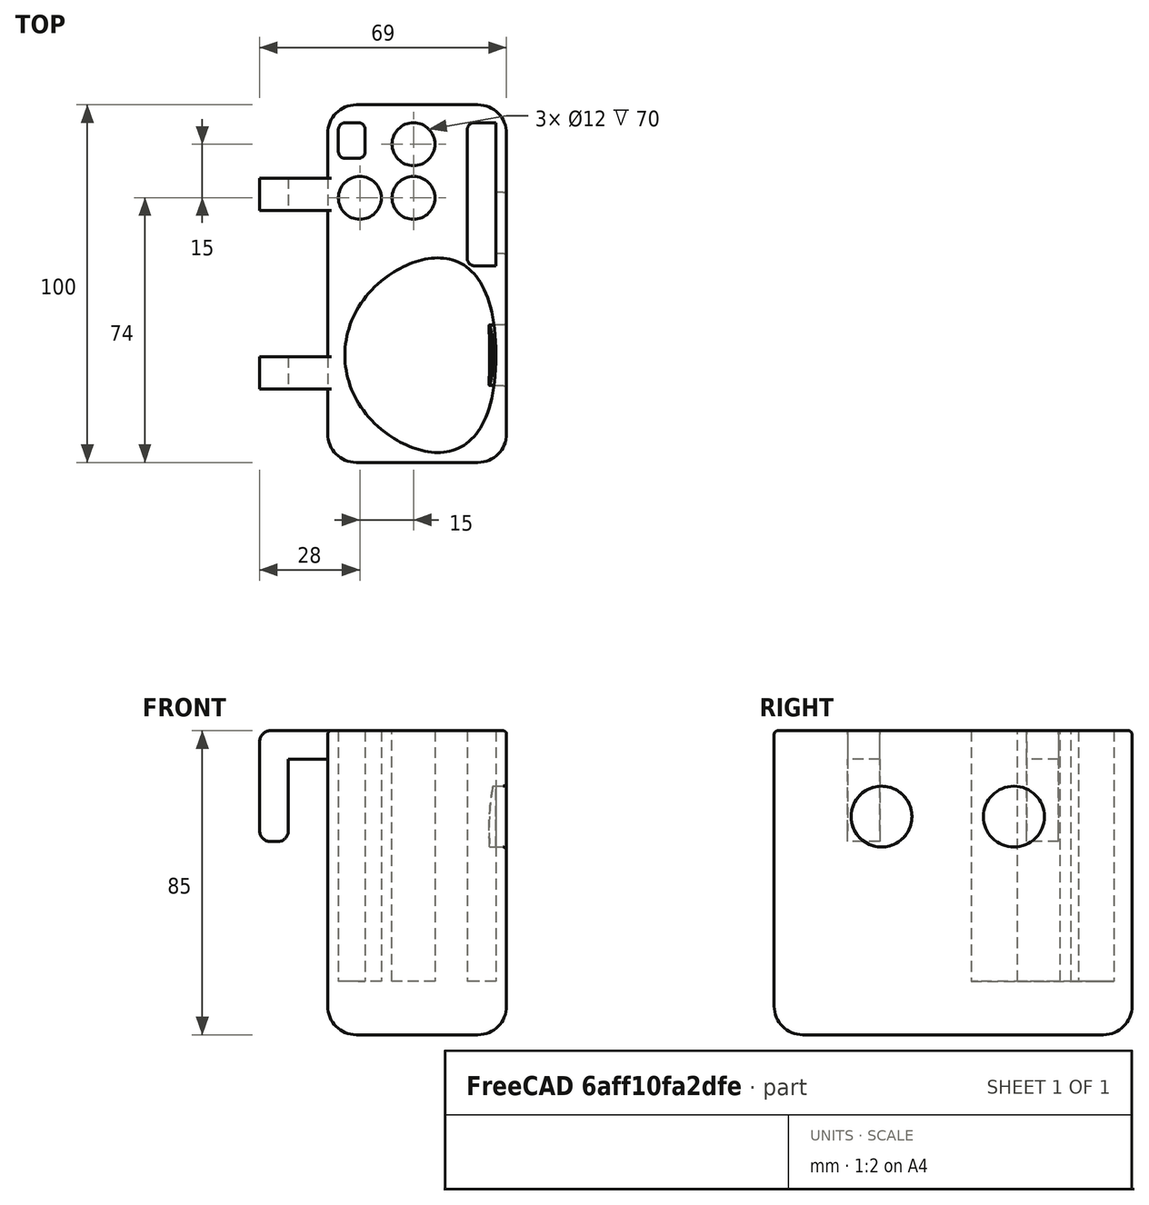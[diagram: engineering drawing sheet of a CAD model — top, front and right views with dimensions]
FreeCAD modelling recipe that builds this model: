
FCSTD DOCUMENT  (FreeCAD 0.20R29177 +426 (Git))
Label: RemoteHolder
License: All rights reserved
LicenseURL: http://en.wikipedia.org/wiki/All_rights_reserved
objects: Sketcher::SketchObject×6, PartDesign::Pocket×5, PartDesign::Fillet×2, Part::Box×1, PartDesign::FeatureBase×1, PartDesign::Pad×1, PartDesign::Body×1, Mesh::Feature×1
note: 25 computed .brp shape members not serialized (recipe doc carries the construction recipe); baked Part::Feature solids carry a one-line shape summary decoded from their .brp

FEATURE [Part::Box] Box  label="Cube"
  AttacherType = Attacher::AttachEngine3D
  Height = 85
  Length = 50
  Width = 100
FEATURE [PartDesign::FeatureBase] BaseFeature
  BaseFeature = -> Box
FEATURE [Sketcher::SketchObject] Sketch
  FullyConstrained = true
  MapMode = 5
  Placement = pos=(0,0,85) rot=(0,0,1;0rad)
  Support = -> [BaseFeature]
  sketch-geometry (15):
    g0-g5: Circle x6 (B-spline internal-alignment scaffolding for g6; pole/knot coordinates omitted)
    g6: BSplineCurve PolesCount=6 KnotsCount=4 Degree=3 IsPeriodic=0
    g7-g10: GeomPoint x4 (B-spline internal-alignment scaffolding for g6; pole/knot coordinates omitted)
    g11: LineSegment StartX=47 StartY=65 StartZ=0 EndX=47 EndY=30 EndZ=0
    g12: LineSegment StartX=47 StartY=30 StartZ=0 EndX=47 EndY=-5 EndZ=0
    g13: LineSegment StartX=47 StartY=30 StartZ=0 EndX=2 EndY=55 EndZ=0
    g14: LineSegment StartX=47 StartY=30 StartZ=0 EndX=2 EndY=5 EndZ=0
  constraints (23):
    c: Equal(g0, g1-g5) x5
    c: Coincident(g6,g0)
    c: InternalAlignment(g0-g5 -> g6) x6
    c: InternalAlignment(g7-g10 -> g6) x4
    c: Vertical(g2,g3)
    c: Vertical(g11)
    c: Coincident(g12,g6)
    c: Coincident(g12,g1)
    c: Vertical(g12)
    c: Coincident(g13,g6)
    c: Coincident(g13,g3)
    c: Coincident(g14,g6)
    c: Coincident(g14,g2)
    c: Equal(g13,g14)
    c: Equal(g11,g12)
    c: Coincident(g11,g6)
    c: Coincident(g11,g4)
    c: DistanceX(g2,g1) = 45
    c: DistanceY(g2,g3) = 50
    c: Weight(g0) = 1
    c: DistanceY(g-1,g2) = 5
    c: DistanceY(g1,g4) = 70
    c: DistanceX(g-1,g2) = 2
FEATURE [Sketcher::SketchObject] Sketch002
  FullyConstrained = true
  MapMode = 5
  Placement = pos=(0,0,85) rot=(0,0,1;0rad)
  Support = -> [BaseFeature]
  sketch-geometry (8):
    g0: LineSegment StartX=47 StartY=95 StartZ=0 EndX=41 EndY=95 EndZ=0
    g1: LineSegment StartX=39 StartY=93 StartZ=0 EndX=39 EndY=57 EndZ=0
    g2: LineSegment StartX=41 StartY=55 StartZ=0 EndX=47 EndY=55 EndZ=0
    g3: LineSegment StartX=47 StartY=55 StartZ=0 EndX=47 EndY=95 EndZ=0
    g4: ArcOfCircle CenterX=41 CenterY=93 CenterZ=0 NormalX=0 NormalY=0 NormalZ=1 AngleXU=0 Radius=2 StartAngle=1.5708 EndAngle=3.14159
    g5: GeomPoint X=39 Y=95 Z=0
    g6: ArcOfCircle CenterX=41 CenterY=57 CenterZ=0 NormalX=0 NormalY=0 NormalZ=1 AngleXU=0 Radius=2 StartAngle=3.14159 EndAngle=4.71239
    g7: GeomPoint X=39 Y=55 Z=0
  constraints (20):
    c: Coincident(g2,g3)
    c: Coincident(g3,g0)
    c: Horizontal(g0)
    c: Horizontal(g2)
    c: Vertical(g1)
    c: Vertical(g3)
    c: DistanceX(g5,g0) = 8
    c: DistanceY(g-1,g0) = 95
    c: DistanceX(g-1,g2) = 47
    c: DistanceY(g3,g3) = 40
    c: PointOnObject(g5,g0)
    c: PointOnObject(g5,g1)
    c: Tangent(g0,g4) = -1.5708
    c: Tangent(g1,g4) = -1.5708
    c: PointOnObject(g7,g1)
    c: PointOnObject(g7,g2)
    c: Tangent(g1,g6) = -1.5708
    c: Tangent(g2,g6) = -1.5708
    c: Equal(g4,g6)
    c: Radius(g4) = 2
FEATURE [PartDesign::Pocket] Pocket002
  BaseFeature = -> BaseFeature
  Direction = (0,0,-1)
  Length = 70
  Length2 = 5
  Profile = -> Sketch002
  ReferenceAxis = -> Sketch002 [N_Axis]
  Type = 0
FEATURE [PartDesign::Pocket] Pocket
  BaseFeature = -> Pocket002
  Direction = (0,0,-1)
  Length = 80
  Length2 = 5
  Profile = -> Sketch
  ReferenceAxis = -> Sketch [N_Axis]
  TaperAngle = -3
  Type = 0
FEATURE [Sketcher::SketchObject] Sketch001
  FullyConstrained = true
  MapMode = 5
  Placement = pos=(50,0,0) rot=(0.57735,0.57735,0.57735;2.0944rad)
  Support = -> [Pocket]
  sketch-geometry (2):
    g0: Circle CenterX=30 CenterY=61 CenterZ=0 NormalX=0 NormalY=0 NormalZ=1 AngleXU=0 Radius=8.5
    g1: Circle CenterX=67 CenterY=61 CenterZ=0 NormalX=0 NormalY=0 NormalZ=1 AngleXU=0 Radius=8.5
  constraints (6):
    c: Diameter(g0) = 17
    c: DistanceY(g-1,g0) = 61
    c: DistanceX(g-1,g0) = 30
    c: Diameter(g1) = 17
    c: DistanceY(g-1,g1) = 61
    c: DistanceX(g-1,g1) = 67
FEATURE [PartDesign::Pocket] Pocket001
  BaseFeature = -> Pocket
  Direction = (-1,0,0)
  Length = 7
  Length2 = 5
  Profile = -> Sketch001
  ReferenceAxis = -> Sketch001 [N_Axis]
  Type = 0
FEATURE [Sketcher::SketchObject] Sketch003
  FullyConstrained = true
  MapMode = 5
  Placement = pos=(0,0,85) rot=(0,0,1;0rad)
  Support = -> [Box]
  sketch-geometry (15):
    g0: ArcOfCircle CenterX=5 CenterY=93 CenterZ=0 NormalX=0 NormalY=0 NormalZ=1 AngleXU=0 Radius=2 StartAngle=1.5708 EndAngle=3.14159
    g1: LineSegment StartX=5 StartY=95 StartZ=0 EndX=8.5 EndY=95 EndZ=0
    g2: ArcOfCircle CenterX=8.5 CenterY=93 CenterZ=0 NormalX=0 NormalY=0 NormalZ=1 AngleXU=0 Radius=2 StartAngle=-1.8e-15 EndAngle=1.5708
    g3: LineSegment StartX=10.5 StartY=93 StartZ=0 EndX=10.5 EndY=87 EndZ=0
    g4: ArcOfCircle CenterX=8.5 CenterY=87 CenterZ=0 NormalX=0 NormalY=0 NormalZ=1 AngleXU=0 Radius=2 StartAngle=4.71239 EndAngle=6.28319
    g5: LineSegment StartX=8.5 StartY=85 StartZ=0 EndX=5 EndY=85 EndZ=0
    g6: ArcOfCircle CenterX=5 CenterY=87 CenterZ=0 NormalX=0 NormalY=0 NormalZ=1 AngleXU=0 Radius=2 StartAngle=3.14159 EndAngle=4.71239
    g7: LineSegment StartX=3 StartY=87 StartZ=0 EndX=3 EndY=93 EndZ=0
    g8: GeomPoint X=3 Y=95 Z=0
    g9: GeomPoint X=10.5 Y=85 Z=0
    g10: Circle CenterX=9 CenterY=74 CenterZ=0 NormalX=0 NormalY=0 NormalZ=1 AngleXU=0 Radius=6
    g11: Circle CenterX=24 CenterY=89 CenterZ=0 NormalX=0 NormalY=0 NormalZ=1 AngleXU=0 Radius=6
    g12: Circle CenterX=24 CenterY=74 CenterZ=0 NormalX=0 NormalY=0 NormalZ=1 AngleXU=0 Radius=6
    g13: LineSegment StartX=9 StartY=74 StartZ=0 EndX=24 EndY=74 EndZ=0
    g14: LineSegment StartX=24 StartY=89 StartZ=0 EndX=24 EndY=74 EndZ=0
  constraints (37):
    c: Tangent(g0,g1) = 1.5708
    c: Tangent(g1,g2) = 1.5708
    c: Tangent(g2,g3) = 1.5708
    c: Tangent(g3,g4) = 1.5708
    c: Tangent(g4,g5) = 1.5708
    c: Tangent(g5,g6) = 1.5708
    c: Tangent(g6,g7) = 1.5708
    c: Tangent(g7,g0) = 1.5708
    c: Horizontal(g1)
    c: Horizontal(g5)
    c: Vertical(g3)
    c: Vertical(g7)
    c: Equal(g0,g2)
    c: Equal(g2,g4)
    c: Equal(g4,g6)
    c: PointOnObject(g8,g1)
    c: PointOnObject(g8,g7)
    c: PointOnObject(g9,g3)
    c: PointOnObject(g9,g5)
    c: DistanceX(g8,g9) = 7.5
    c: DistanceY(g9,g8) = 10
    c: Radius(g0) = 2
    c: DistanceY(g-1,g8) = 95
    c: DistanceX(g-1,g8) = 3
    c: Equal(g11,g12)
    c: Equal(g10,g12)
    c: Radius(g11) = 6
    c: Vertical(g11,g12)
    c: Horizontal(g10,g12)
    c: Tangent(g7,g10)
    c: Tangent(g1,g11)
    c: Coincident(g13,g10)
    c: Coincident(g13,g12)
    c: Coincident(g14,g11)
    c: Coincident(g14,g12)
    c: Equal(g14,g13)
    c: DistanceX(g13,g13) = 15
FEATURE [PartDesign::Pocket] Pocket003
  BaseFeature = -> Pocket001
  Direction = (0,0,-1)
  Length = 70
  Length2 = 5
  Profile = -> Sketch003
  ReferenceAxis = -> Sketch003 [N_Axis]
  Type = 0
FEATURE [Sketcher::SketchObject] Sketch004
  AttachmentOffset = pos=(0,0,-50) rot=(0,0,1;0rad)
  FullyConstrained = true
  MapMode = 5
  Placement = pos=(0,50,1.11e-14) rot=(1,0,0;1.5708rad)
  Support = -> [XZ_Plane]
  sketch-geometry (12):
    g0: LineSegment StartX=0 StartY=85 StartZ=0 EndX=-16 EndY=85 EndZ=0
    g1: LineSegment StartX=-19 StartY=82 StartZ=0 EndX=-19 EndY=57 EndZ=0
    g2: LineSegment StartX=-16 StartY=54 StartZ=0 EndX=-14 EndY=54 EndZ=0
    g3: LineSegment StartX=-11 StartY=57 StartZ=0 EndX=-11 EndY=77 EndZ=0
    g4: LineSegment StartX=-11 StartY=77 StartZ=0 EndX=0 EndY=77 EndZ=0
    g5: ArcOfCircle CenterX=-16 CenterY=82 CenterZ=0 NormalX=0 NormalY=0 NormalZ=1 AngleXU=0 Radius=3 StartAngle=1.5708 EndAngle=3.14159
    g6: GeomPoint X=-19 Y=85 Z=0
    g7: ArcOfCircle CenterX=-16 CenterY=57 CenterZ=0 NormalX=0 NormalY=0 NormalZ=1 AngleXU=0 Radius=3 StartAngle=3.14159 EndAngle=4.71239
    g8: GeomPoint X=-19 Y=54 Z=0
    g9: ArcOfCircle CenterX=-14 CenterY=57 CenterZ=0 NormalX=0 NormalY=0 NormalZ=1 AngleXU=0 Radius=3 StartAngle=4.71239 EndAngle=6.28319
    g10: GeomPoint X=-11 Y=54 Z=0
    g11: LineSegment StartX=0 StartY=85 StartZ=0 EndX=0 EndY=77 EndZ=0
  constraints (30):
    c: PointOnObject(g0,g-2)
    c: Horizontal(g0)
    c: Vertical(g1)
    c: Horizontal(g2)
    c: Vertical(g3)
    c: Coincident(g3,g4)
    c: Horizontal(g4)
    c: PointOnObject(g4,g-2)
    c: DistanceY(g10,g3) = 23
    c: DistanceX(g4,g4) = 11
    c: DistanceX(g8,g10) = 8
    c: DistanceY(g4,g0) = 8
    c: DistanceY(g-1,g0) = 85
    c: PointOnObject(g6,g0)
    c: PointOnObject(g6,g1)
    c: Tangent(g0,g5) = -1.5708
    c: Tangent(g1,g5) = -1.5708
    c: PointOnObject(g8,g1)
    c: PointOnObject(g8,g2)
    c: Tangent(g1,g7) = -1.5708
    c: Tangent(g2,g7) = -1.5708
    c: PointOnObject(g10,g2)
    c: PointOnObject(g10,g3)
    c: Tangent(g2,g9) = -1.5708
    c: Tangent(g3,g9) = -1.5708
    c: Equal(g5,g7)
    c: Equal(g9,g7)
    c: Radius(g5) = 3
    c: Coincident(g11,g0)
    c: Coincident(g11,g4)
FEATURE [PartDesign::Pad] Pad
  BaseFeature = -> Pocket003
  Direction = (0,-1,-2e-16)
  Length = 59
  Length2 = 10
  Midplane = true
  Profile = -> Sketch004
  ReferenceAxis = -> Sketch004 [N_Axis]
  Type = 0
FEATURE [Sketcher::SketchObject] Sketch005
  FullyConstrained = true
  MapMode = 5
  Support = -> [XY_Plane]
  sketch-geometry (4):
    g0: LineSegment StartX=0 StartY=70.5 StartZ=0 EndX=-25 EndY=70.5 EndZ=0
    g1: LineSegment StartX=-25 StartY=70.5 StartZ=0 EndX=-25 EndY=29.5 EndZ=0
    g2: LineSegment StartX=-25 StartY=29.5 StartZ=0 EndX=0 EndY=29.5 EndZ=0
    g3: LineSegment StartX=0 StartY=29.5 StartZ=0 EndX=0 EndY=70.5 EndZ=0
  constraints (12):
    c: Coincident(g0,g1)
    c: Coincident(g1,g2)
    c: Coincident(g2,g3)
    c: Coincident(g3,g0)
    c: Horizontal(g0)
    c: Horizontal(g2)
    c: Vertical(g1)
    c: Vertical(g3)
    c: PointOnObject(g0,g-2)
    c: DistanceY(g1,g1) = 41
    c: DistanceX(g2,g2) = 25
    c: DistanceY(g-1,g1) = 29.5
FEATURE [PartDesign::Pocket] Pocket004
  BaseFeature = -> Pad
  Direction = (0,0,-1)
  Length = 85
  Length2 = 5
  Profile = -> Sketch005
  ReferenceAxis = -> Sketch005 [N_Axis]
  Reversed = true
  Type = 0
FEATURE [PartDesign::Fillet] Fillet
  Base = -> Pocket004 [Edge54,Edge53,Edge6,Edge52,Edge65,Edge51,Edge50,Edge49,Edge5,Edge64]
  BaseFeature = -> Pocket004
  Radius = 8
  SupportTransform = false
  UseAllEdges = false
FEATURE [PartDesign::Fillet] Fillet002
  Base = -> Fillet [Edge10,Edge1,Edge7,Edge9,Edge11,Edge13,Edge15,Edge17,Edge16,Edge14,Edge73,Edge72]
  BaseFeature = -> Fillet
  Radius = 1
  SupportTransform = false
  UseAllEdges = false
FEATURE [PartDesign::Body] Body
  BaseFeature = -> Box
  Group = -> [BaseFeature,Sketch,Sketch002,Pocket002,Pocket,Sketch001,Pocket001,Sketch003,Pocket003,Sketch004,Pad,Sketch005,Pocket004,Fillet,Fillet002]
  Origin = -> Origin
  Tip = -> Fillet002
FEATURE [Mesh::Feature] Mesh  label="Body (Meshed)"
